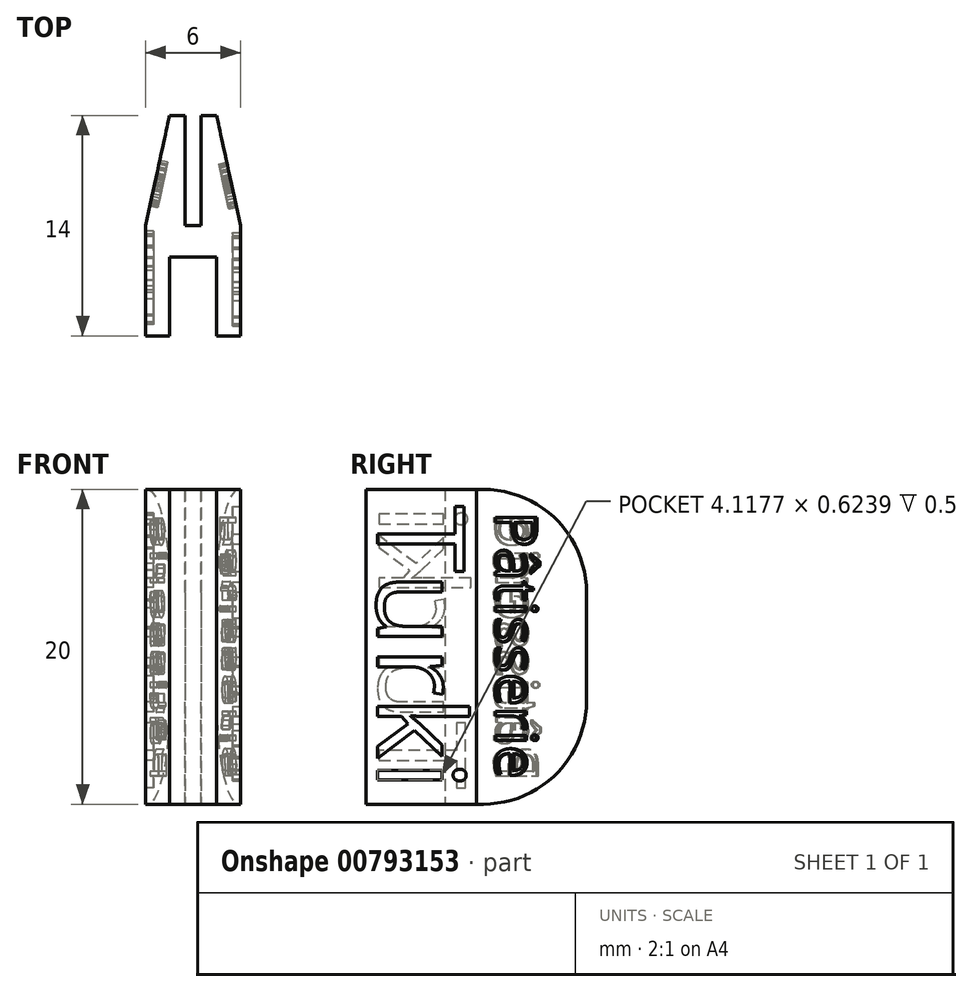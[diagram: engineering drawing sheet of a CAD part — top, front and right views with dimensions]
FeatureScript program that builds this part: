
annotation { "Feature Type Name" : "Feature", "Feature Type Description" : "" }
export const myFeature = defineFeature(function(context is Context, id is Id, definition is map)
    precondition{}
    {
        {
            var Q0;
            Q0=qCreatedBy(makeId("Top.planeOp"),FACE);
            var sketch = newSketch(context, id + "F0", { "sketchPlane" : qUnion([Q0])});
            skLineSegment(sketch, "E0", {"start": v(1.5, 0) * mm, "end": v(3, 0) * mm});
            skLineSegment(sketch, "E1", {"start": v(3, 0) * mm, "end": v(3, 7) * mm});
            skLineSegment(sketch, "E2", {"start": v(3, 7) * mm, "end": v(1.5, 14) * mm});
            skLineSegment(sketch, "E3", {"start": v(1.5, 14) * mm, "end": v(0.5, 14) * mm});
            skLineSegment(sketch, "E4", {"start": v(0.5, 14) * mm, "end": v(0.5, 7) * mm});
            skLineSegment(sketch, "E5", {"start": v(0.5, 7) * mm, "end": v(0, 7) * mm});
            skLineSegment(sketch, "E6.MirrorCS", {"start": v(-0.5, 7) * mm, "end": v(0, 7) * mm});
            skLineSegment(sketch, "E7.MirrorCS", {"start": v(-0.5, 14) * mm, "end": v(-0.5, 7) * mm});
            skLineSegment(sketch, "E8.MirrorCS", {"start": v(-1.5, 14) * mm, "end": v(-0.5, 14) * mm});
            skLineSegment(sketch, "E9.MirrorCS", {"start": v(-3, 7) * mm, "end": v(-1.5, 14) * mm});
            skLineSegment(sketch, "E10.MirrorCS", {"start": v(-3, 0) * mm, "end": v(-3, 7) * mm});
            skLineSegment(sketch, "E11.MirrorCS", {"start": v(-1.5, 0) * mm, "end": v(-3, 0) * mm});
            skLineSegment(sketch, "E12", {"start": v(1.5, 0) * mm, "end": v(1.5, 5) * mm});
            skLineSegment(sketch, "E13", {"start": v(1.5, 5) * mm, "end": v(0, 5) * mm});
            skLineSegment(sketch, "E14.MirrorCS", {"start": v(-1.5, 5) * mm, "end": v(0, 5) * mm});
            skLineSegment(sketch, "E15.MirrorCS", {"start": v(-1.5, 0) * mm, "end": v(-1.5, 5) * mm});
            skSolve(sketch);
        }
        {
            var Q0;
            Q0 = qSketchRegion(id + "F0", true);
            extrude(context, id + "F1", {"entities" : qUnion([Q0]), "depth" : 20 * mm, "offsetDistance" : 25 * mm});
        }
        {
            var Q0;
            Q0=makeQuery(id+"F1.opExtrude","CAP_EDGE",EDGE,{"disambiguationData":[OSD([sQuery(id+"F0.wireOp",EDGE,"E3")])],"isStart":true});
            var Q1;
            Q1=makeQuery(id+"F1.opExtrude","CAP_EDGE",EDGE,{"disambiguationData":[OSD([sQuery(id+"F0.wireOp",EDGE,"E3")])],"isStart":false});
            var Q2;
            Q2=makeQuery(id+"F1.opExtrude","CAP_EDGE",EDGE,{"disambiguationData":[OSD([sQuery(id+"F0.wireOp",EDGE,"E8.MirrorCS")])],"isStart":true});
            var Q3;
            Q3=makeQuery(id+"F1.opExtrude","CAP_EDGE",EDGE,{"disambiguationData":[OSD([sQuery(id+"F0.wireOp",EDGE,"E8.MirrorCS")])],"isStart":false});
            fillet(context, id + "F2", {"entities" : qUnion([Q0, Q1, Q2, Q3]), "radius" : 6.57 * mm, "tangentPropagation" : true, "allowEdgeOverflow" : false});
        }
        {
            var Q0;
            Q0=makeQuery(id+"F1.opExtrude","SWEPT_FACE",FACE,{"disambiguationData":[OSD([sQuery(id+"F0.wireOp",EDGE,"E1")])]});
            var sketch = newSketch(context, id + "F3", { "sketchPlane" : qUnion([Q0])});
            skText(sketch, "E16", { "text": "Turki", "fontName": "OpenSans-Regular.ttf"});
            const initialGuessF3  = {"E16": [0.0007, 0.01898, 0, -1, 0.00554]};
            skSetInitialGuess(sketch, initialGuessF3);
            skSolve(sketch);
        }
        {
            var Q0;
            Q0 = qSketchRegion(id + "F3", true);
            extrude(context, id + "F4", {"entities" : qUnion([Q0]), "operationType" : NewBodyOperationType.REMOVE, "oppositeDirection" : true, "depth" : 0.5 * mm, "offsetDistance" : 25 * mm});
        }
        {
            var Q0;
            Q0=makeQuery(id+"F1.opExtrude","SWEPT_FACE",FACE,{"disambiguationData":[OSD([sQuery(id+"F0.wireOp",EDGE,"E10.MirrorCS")])]});
            var sketch = newSketch(context, id + "F5", { "sketchPlane" : qUnion([Q0])});
            skText(sketch, "E17", { "text": "Turki", "fontName": "OpenSans-Regular.ttf"});
            const initialGuessF5  = {"E17": [-0.0008, 0.00098, 0, 1, 0.00554]};
            skSetInitialGuess(sketch, initialGuessF5);
            skSolve(sketch);
        }
        {
            var Q0;
            Q0 = qSketchRegion(id + "F5", true);
            extrude(context, id + "F6", {"entities" : qUnion([Q0]), "operationType" : NewBodyOperationType.REMOVE, "oppositeDirection" : true, "depth" : 0.5 * mm, "offsetDistance" : 25 * mm});
        }
        {
            var Q0;
            Q0=makeQuery(id+"F1.opExtrude","SWEPT_FACE",FACE,{"disambiguationData":[OSD([sQuery(id+"F0.wireOp",EDGE,"E9.MirrorCS")])]});
            var sketch = newSketch(context, id + "F7", { "sketchPlane" : qUnion([Q0])});
            skText(sketch, "E18", { "text": "Pâtisserie", "fontName": "OpenSans-Regular.ttf"});
            const initialGuessF7  = {"E18": [-0.00755, 0.00141, 0, 1, 0.00271]};
            skSetInitialGuess(sketch, initialGuessF7);
            skSolve(sketch);
        }
        {
            var Q0;
            Q0 = qSketchRegion(id + "F7", true);
            extrude(context, id + "F8", {"entities" : qUnion([Q0]), "operationType" : NewBodyOperationType.REMOVE, "oppositeDirection" : true, "depth" : 0.5 * mm, "offsetDistance" : 25 * mm});
        }
        {
            var Q0;
            Q0=makeQuery(id+"F1.opExtrude","SWEPT_FACE",FACE,{"disambiguationData":[OSD([sQuery(id+"F0.wireOp",EDGE,"E2")])]});
            var sketch = newSketch(context, id + "F9", { "sketchPlane" : qUnion([Q0])});
            skText(sketch, "E19", { "text": "Pâtisserie", "fontName": "OpenSans-Regular.ttf"});
            const initialGuessF9  = {"E19": [0.00745, 0.01857, 0, -1, 0.00271]};
            skSetInitialGuess(sketch, initialGuessF9);
            skSolve(sketch);
        }
        {
            var Q0;
            Q0 = qSketchRegion(id + "F9", true);
            extrude(context, id + "F10", {"entities" : qUnion([Q0]), "operationType" : NewBodyOperationType.REMOVE, "oppositeDirection" : true, "depth" : 0.5 * mm, "offsetDistance" : 25 * mm});
        }
        {
            var Q0;
            Q0 = qSketchRegion(id + "F9", true);
            extrude(context, id + "F11", {"entities" : qUnion([Q0]), "operationType" : NewBodyOperationType.REMOVE, "oppositeDirection" : true, "depth" : 0.5 * mm, "offsetDistance" : 25 * mm});
        }
    });
